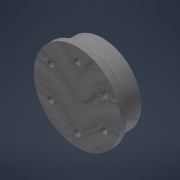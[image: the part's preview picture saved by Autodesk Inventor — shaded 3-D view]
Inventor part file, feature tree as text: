
AUTODESK INVENTOR PART (.ipt)
format: ipt  version: 2022 (Build 260153000, 153)  size: 168,448 bytes
history: native  units: mm
features: reference x7, sketch x6, extrude x4, chamfer x2, projected_geometry x2, other x2, plane x1, hole x1, pattern_circular x1
ambient origin geometry x8: Origin, YZ Plane, XZ Plane, XY Plane, X Axis, Y Axis, Z Axis, Center Point
bodies: Solid1 (feature_tree)
feature tree (26):
  sketch  "Sketch1"  dims[d2=10.0mm d3=0.0mm d4=45.0mm]
  extrude  "Extrusion1"  Depth=10.0mm
  extrude  "Extrusion2"  Depth=3.0mm TaperAngle=0.0deg
  plane  "Work Plane1"
  extrude  "Extrusion3"  Depth=32.0mm
  sketch  "Sketch5"  dims[d16=3.242mm d17=10.0mm d18=4.0mm d19=2.0mm d20=90.0deg d21=11.0mm d22=20.594885mm d23=60.0mm d24=360.0deg]
  chamfer  "Chamfer2"  Distance=60.0mm Angle=360.0deg
  hole  "Hole1"  [1 undecoded]
  pattern_circular  "Circular Pattern1"  [2 undecoded]
  extrude  "Extrusion4"  [1 undecoded]
  chamfer  "Chamfer3"  [1 undecoded]
  sketch  "Sketch2"  dims[d5=3.0mm d6=0.0mm d7=3.0mm d8=0.0mm]
  reference  "Reference1"
  sketch  "Sketch3"  dims[d12=2.0mm d13=2.0mm d14=45.0deg d15=32.0mm]
  reference  "Reference2"
  reference  "Reference3"
  reference  "Reference4"
  reference  "Reference5"
  projected_geometry  "Projected Loop1"
  projected_geometry  "Projected Loop2"
  sketch  "Sketch6"  dims[d26=40.0mm d27=10.0mm d28=0.0mm]
  sketch  "Sketch7"  dims[d29=2.0mm d30=2.0mm d31=45.0deg]
  reference  "Reference6"
  reference  "Reference7"
  other  "SistemaElevacionV2.iam"
  other  "Tornillo de elevación:1"
note: 5 required parameter values undecoded (feature->parameter linkage not recoverable at this tier; creation-order binding heuristic only, values carry confidence <= 0.55)
